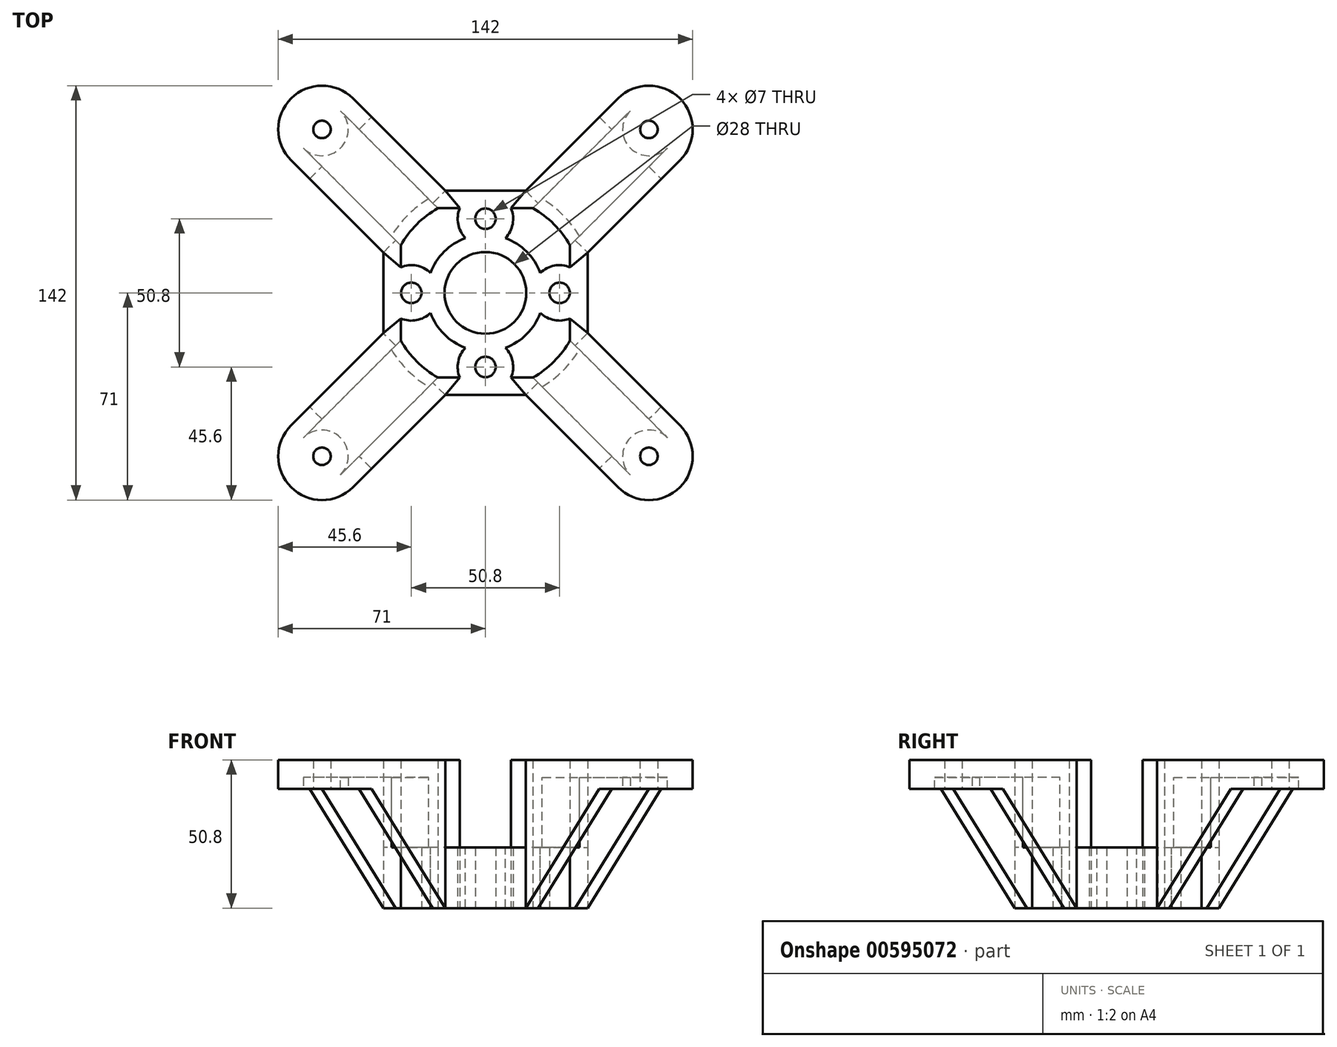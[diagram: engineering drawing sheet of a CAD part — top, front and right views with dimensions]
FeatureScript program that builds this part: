
annotation { "Feature Type Name" : "Feature", "Feature Type Description" : "" }
export const myFeature = defineFeature(function(context is Context, id is Id, definition is map)
    precondition{}
    {
        {
            var Q0;
            Q0=qCreatedBy(makeId("Top.planeOp"),FACE);
            var sketch = newSketch(context, id + "F0", { "sketchPlane" : qUnion([Q0])});
            skCircle(sketch, "E0", {"center": v(0, 0) * mm, "radius": 14 * mm});
            skCircle(sketch, "E1", {"center": v(0, 0) * mm, "radius": 25.4 * mm});
            skLineSegment(sketch, "E2", {"start": v(0, 0) * mm, "end": v(0, 25.4) * mm, "construction": true});
            skLineSegment(sketch, "E3", {"start": v(0, 0) * mm, "end": v(0, -25.4) * mm, "construction": true});
            skCircle(sketch, "E4", {"center": v(0, 25.4) * mm, "radius": 3.5 * mm});
            skLineSegment(sketch, "E5", {"start": v(0, 0) * mm, "end": v(25.4, 0) * mm, "construction": true});
            skCircle(sketch, "E6.MirrorC", {"center": v(0, -25.4) * mm, "radius": 3.5 * mm});
            skLineSegment(sketch, "E7.bottom", {"start": v(-35, 35) * mm, "end": v(35, 35) * mm});
            skLineSegment(sketch, "E7.top", {"start": v(-35, -35) * mm, "end": v(35, -35) * mm});
            skLineSegment(sketch, "E7.left", {"start": v(-35, 35) * mm, "end": v(-35, -35) * mm});
            skLineSegment(sketch, "E7.right", {"start": v(35, 35) * mm, "end": v(35, -35) * mm});
            skCircle(sketch, "E8", {"center": v(25.4, 0) * mm, "radius": 3.5 * mm});
            skCircle(sketch, "E9.MirrorC", {"center": v(-25.4, 0) * mm, "radius": 3.5 * mm});
            skLineSegment(sketch, "E10.bottom", {"start": v(-56, -56) * mm, "end": v(56, -56) * mm, "construction": true});
            skLineSegment(sketch, "E10.top", {"start": v(-56, 56) * mm, "end": v(56, 56) * mm, "construction": true});
            skLineSegment(sketch, "E10.left", {"start": v(-56, -56) * mm, "end": v(-56, 56) * mm, "construction": true});
            skLineSegment(sketch, "E10.right", {"start": v(56, -56) * mm, "end": v(56, 56) * mm, "construction": true});
            skLineSegment(sketch, "E11", {"start": v(0, 0) * mm, "end": v(-56, 56) * mm, "construction": true});
            skLineSegment(sketch, "E12.0", {"start": v(-13.79, 35) * mm, "end": v(-45.4, 66.6) * mm});
            skLineSegment(sketch, "E13.0", {"start": v(-35, 13.79) * mm, "end": v(-66.6, 45.4) * mm});
            skArc(sketch, "E14", {"start": v(-45.4, 66.6) * mm, "mid": v(-66.6, 66.6) * mm, "end": v(-66.6, 45.4) * mm});
            skCircle(sketch, "E15", {"center": v(-56, 56) * mm, "radius": 3 * mm});
            skLineSegment(sketch, "E16.MirrorCS", {"start": v(13.79, 35) * mm, "end": v(45.4, 66.6) * mm});
            skArc(sketch, "E17.MirrorCS", {"start": v(45.4, 66.6) * mm, "mid": v(66.6, 66.6) * mm, "end": v(66.6, 45.4) * mm});
            skLineSegment(sketch, "E18.MirrorCS", {"start": v(35, 13.79) * mm, "end": v(66.6, 45.4) * mm});
            skCircle(sketch, "E19.MirrorC", {"center": v(56, 56) * mm, "radius": 3 * mm});
            skLineSegment(sketch, "E20.MirrorCS", {"start": v(-13.79, -35) * mm, "end": v(-45.4, -66.6) * mm});
            skArc(sketch, "E21.MirrorCS", {"start": v(-45.4, -66.6) * mm, "mid": v(-66.6, -66.6) * mm, "end": v(-66.6, -45.4) * mm});
            skLineSegment(sketch, "E22.MirrorCS", {"start": v(-35, -13.79) * mm, "end": v(-66.6, -45.4) * mm});
            skCircle(sketch, "E23.MirrorC", {"center": v(-56, -56) * mm, "radius": 3 * mm});
            skCircle(sketch, "E24.MirrorC", {"center": v(56, -56) * mm, "radius": 3 * mm});
            skArc(sketch, "E25.MirrorCS", {"start": v(45.4, -66.6) * mm, "mid": v(66.6, -66.6) * mm, "end": v(66.6, -45.4) * mm});
            skLineSegment(sketch, "E26.MirrorCS", {"start": v(13.79, -35) * mm, "end": v(45.4, -66.6) * mm});
            skLineSegment(sketch, "E27.MirrorCS", {"start": v(35, -13.79) * mm, "end": v(66.6, -45.4) * mm});
            skSolve(sketch);
        }
        {
            var Q0;
            Q0=qSketchRegion(id+"F0",true);
            var Q1;
            Q1=makeQuery(id+"F0.imprint","IMPRINT",FACE,{"disambiguationData":[TD([[makeQuery(id+"F0.imprint","IMPRINT",EDGE,{"derivedFrom":sQuery(id+"F0.wireOp",EDGE,"E0")}),-1.0]])]});
            extrude(context, id + "F1", {"entities" : qUnion([Q0, Q1]), "depth" : 50.8 * mm});
        }
        {
            var Q0;
            Q0=makeQuery(id+"F1.opExtrude","CAP_FACE",FACE,{"disambiguationData":[OSD([sQuery(id+"F0.wireOp",EDGE,"E0"),sQuery(id+"F0.wireOp",EDGE,"E4"),sQuery(id+"F0.wireOp",EDGE,"E6.MirrorC"),sQuery(id+"F0.wireOp",EDGE,"E7.bottom"),sQuery(id+"F0.wireOp",EDGE,"E7.top"),sQuery(id+"F0.wireOp",EDGE,"E7.left"),sQuery(id+"F0.wireOp",EDGE,"E7.right"),sQuery(id+"F0.wireOp",EDGE,"E8"),sQuery(id+"F0.wireOp",EDGE,"E9.MirrorC"),sQuery(id+"F0.wireOp",EDGE,"E12.0"),sQuery(id+"F0.wireOp",EDGE,"E13.0"),sQuery(id+"F0.wireOp",EDGE,"E14"),sQuery(id+"F0.wireOp",EDGE,"E15"),sQuery(id+"F0.wireOp",EDGE,"E16.MirrorCS"),sQuery(id+"F0.wireOp",EDGE,"E17.MirrorCS"),sQuery(id+"F0.wireOp",EDGE,"E18.MirrorCS"),sQuery(id+"F0.wireOp",EDGE,"E19.MirrorC"),sQuery(id+"F0.wireOp",EDGE,"E20.MirrorCS"),sQuery(id+"F0.wireOp",EDGE,"E21.MirrorCS"),sQuery(id+"F0.wireOp",EDGE,"E22.MirrorCS"),sQuery(id+"F0.wireOp",EDGE,"E23.MirrorC"),sQuery(id+"F0.wireOp",EDGE,"E24.MirrorC"),sQuery(id+"F0.wireOp",EDGE,"E25.MirrorCS"),sQuery(id+"F0.wireOp",EDGE,"E26.MirrorCS"),sQuery(id+"F0.wireOp",EDGE,"E27.MirrorCS")])],"isStart":true});
            shell(context, id + "F2", {"entities" : qUnion([Q0]), "thickness" : 6 * mm});
        }
        {
            var Q0;
            Q0=makeQuery(id+"F1.opExtrude","SWEPT_FACE",FACE,{"disambiguationData":[OSD([sQuery(id+"F0.wireOp",EDGE,"E26.MirrorCS")])]});
            var sketch = newSketch(context, id + "F3", { "sketchPlane" : qUnion([Q0])});
            skLineSegment(sketch, "E28", {"start": v(94.2, 40.8) * mm, "end": v(94.2, 40.8) * mm});
            skLineSegment(sketch, "E29", {"start": v(94.2, 40.8) * mm, "end": v(34.5, 40.8) * mm});
            skLineSegment(sketch, "E30", {"start": v(34.5, 40.8) * mm, "end": v(34.5, 0) * mm});
            skPoint(sketch, "E31.0", {"position": v(94.2, 0) * mm});
            skPoint(sketch, "E32.0", {"position": v(94.2, 50.8) * mm});
            skLineSegment(sketch, "E33", {"start": v(34.5, 0) * mm, "end": v(94.2, 0) * mm});
            skPoint(sketch, "E34.0", {"position": v(70.2, 0) * mm});
            skLineSegment(sketch, "E35", {"start": v(70.2, 0) * mm, "end": v(70.2, 40.8) * mm});
            skLineSegment(sketch, "E36", {"start": v(70.2, 40.8) * mm, "end": v(34.5, 0) * mm});
            skLineSegment(sketch, "E37", {"start": v(94.2, 0) * mm, "end": v(94.2, 40.8) * mm});
            skSolve(sketch);
        }
        {
            var Q0;
            {var subQ0=sQuery(id+"F3.wireOp",EDGE,"E37");Q0=makeQuery(id+"F3.imprint","IMPRINT",FACE,{"disambiguationData":[TD([[makeQuery(id+"F3.imprint","IMPRINT",EDGE,{"derivedFrom":subQ0}),1.0]])]});}
            var Q1;
            {var subQ0=sQuery(id+"F3.wireOp",EDGE,"E35");Q1=makeQuery(id+"F3.imprint","IMPRINT",FACE,{"disambiguationData":[TD([[makeQuery(id+"F3.imprint","IMPRINT",EDGE,{"derivedFrom":subQ0}),-1.0]])]});}
            var Q2;
            {var subQ2=sQuery(id+"F3.wireOp",EDGE,"E35");Q2=makeQuery(id+"F3.imprint","IMPRINT",FACE,{"disambiguationData":[TD([[makeQuery(id+"F3.imprint","IMPRINT",EDGE,{"derivedFrom":subQ2}),1.0]])]});}
            extrude(context, id + "F4", {"entities" : qUnion([Q0, Q1, Q2]), "operationType" : NewBodyOperationType.REMOVE, "endBound" : BoundingType.THROUGH_ALL, "oppositeDirection" : true, "depth" : 25.4 * mm});
        }
        {
            var Q0;
            Q0=makeQuery(id+"F1.opExtrude","SWEPT_FACE",FACE,{"disambiguationData":[OSD([sQuery(id+"F0.wireOp",EDGE,"E18.MirrorCS")])]});
            var sketch = newSketch(context, id + "F5", { "sketchPlane" : qUnion([Q0])});
            skPoint(sketch, "E38.0", {"position": v(94.2, 0) * mm});
            skPoint(sketch, "E39.0", {"position": v(70.2, 0) * mm});
            skPoint(sketch, "E40.0", {"position": v(94.2, 50.8) * mm});
            skLineSegment(sketch, "E41", {"start": v(94.2, 0) * mm, "end": v(94.2, 40.8) * mm});
            skLineSegment(sketch, "E42", {"start": v(94.2, 0) * mm, "end": v(34.5, 0) * mm});
            skLineSegment(sketch, "E43", {"start": v(70.2, 0) * mm, "end": v(70.2, 40.8) * mm});
            skLineSegment(sketch, "E44", {"start": v(94.2, 40.8) * mm, "end": v(34.5, 40.8) * mm});
            skLineSegment(sketch, "E45", {"start": v(34.5, 40.8) * mm, "end": v(34.5, 0) * mm});
            skLineSegment(sketch, "E46", {"start": v(70.2, 40.8) * mm, "end": v(34.5, 0) * mm});
            skSolve(sketch);
        }
        {
            var Q0;
            {var subQ0=sQuery(id+"F5.wireOp",EDGE,"E41");Q0=makeQuery(id+"F5.imprint","IMPRINT",FACE,{"disambiguationData":[TD([[makeQuery(id+"F5.imprint","IMPRINT",EDGE,{"derivedFrom":subQ0}),1.0]])]});}
            var Q1;
            {var subQ3=sQuery(id+"F5.wireOp",EDGE,"E43");Q1=makeQuery(id+"F5.imprint","IMPRINT",FACE,{"disambiguationData":[TD([[makeQuery(id+"F5.imprint","IMPRINT",EDGE,{"derivedFrom":subQ3}),-1.0]])]});}
            var Q2;
            {var subQ2=sQuery(id+"F5.wireOp",EDGE,"E43");Q2=makeQuery(id+"F5.imprint","IMPRINT",FACE,{"disambiguationData":[TD([[makeQuery(id+"F5.imprint","IMPRINT",EDGE,{"derivedFrom":subQ2}),1.0]])]});}
            extrude(context, id + "F6", {"entities" : qUnion([Q0, Q1, Q2]), "operationType" : NewBodyOperationType.REMOVE, "endBound" : BoundingType.THROUGH_ALL, "oppositeDirection" : true, "depth" : 25.4 * mm});
        }
        {
            var Q0;
            Q0=makeQuery(id+"F1.opExtrude","SWEPT_FACE",FACE,{"disambiguationData":[OSD([sQuery(id+"F0.wireOp",EDGE,"E12.0")])]});
            var sketch = newSketch(context, id + "F7", { "sketchPlane" : qUnion([Q0])});
            skPoint(sketch, "E47.0", {"position": v(94.2, 0) * mm});
            skPoint(sketch, "E48.0", {"position": v(94.2, 50.8) * mm});
            skPoint(sketch, "E49.0", {"position": v(70.2, 0) * mm});
            skLineSegment(sketch, "E50", {"start": v(94.2, 0) * mm, "end": v(34.5, 0) * mm});
            skLineSegment(sketch, "E51", {"start": v(34.5, 0) * mm, "end": v(34.5, 40.8) * mm});
            skLineSegment(sketch, "E52", {"start": v(94.2, 0) * mm, "end": v(94.2, 40.8) * mm});
            skLineSegment(sketch, "E53", {"start": v(94.2, 40.8) * mm, "end": v(34.5, 40.8) * mm});
            skLineSegment(sketch, "E54", {"start": v(70.2, 0) * mm, "end": v(70.2, 40.8) * mm});
            skLineSegment(sketch, "E55", {"start": v(70.2, 40.8) * mm, "end": v(34.5, 0) * mm});
            skSolve(sketch);
        }
        {
            var Q0;
            {var subQ3=sQuery(id+"F7.wireOp",EDGE,"E52");Q0=makeQuery(id+"F7.imprint","IMPRINT",FACE,{"disambiguationData":[TD([[makeQuery(id+"F7.imprint","IMPRINT",EDGE,{"derivedFrom":subQ3}),1.0]])]});}
            var Q1;
            {var subQ3=sQuery(id+"F7.wireOp",EDGE,"E54");Q1=makeQuery(id+"F7.imprint","IMPRINT",FACE,{"disambiguationData":[TD([[makeQuery(id+"F7.imprint","IMPRINT",EDGE,{"derivedFrom":subQ3}),-1.0]])]});}
            var Q2;
            {var subQ2=sQuery(id+"F7.wireOp",EDGE,"E54");Q2=makeQuery(id+"F7.imprint","IMPRINT",FACE,{"disambiguationData":[TD([[makeQuery(id+"F7.imprint","IMPRINT",EDGE,{"derivedFrom":subQ2}),1.0]])]});}
            extrude(context, id + "F8", {"entities" : qUnion([Q0, Q1, Q2]), "operationType" : NewBodyOperationType.REMOVE, "endBound" : BoundingType.THROUGH_ALL, "oppositeDirection" : true, "depth" : 25.4 * mm});
        }
        {
            var Q0;
            Q0=makeQuery(id+"F1.opExtrude","SWEPT_FACE",FACE,{"disambiguationData":[OSD([sQuery(id+"F0.wireOp",EDGE,"E22.MirrorCS")])]});
            var sketch = newSketch(context, id + "F9", { "sketchPlane" : qUnion([Q0])});
            skPoint(sketch, "E56.0", {"position": v(94.2, 0) * mm});
            skPoint(sketch, "E56.1", {"position": v(70.2, 0) * mm});
            skPoint(sketch, "E56.2", {"position": v(94.2, 50.8) * mm});
            skLineSegment(sketch, "E57", {"start": v(94.2, 0) * mm, "end": v(34.5, 0) * mm});
            skLineSegment(sketch, "E58", {"start": v(34.5, 0) * mm, "end": v(34.5, 40.8) * mm});
            skLineSegment(sketch, "E59", {"start": v(94.2, 0) * mm, "end": v(94.2, 40.8) * mm});
            skLineSegment(sketch, "E60", {"start": v(94.2, 40.8) * mm, "end": v(34.5, 40.8) * mm});
            skLineSegment(sketch, "E61", {"start": v(70.2, 0) * mm, "end": v(70.2, 40.8) * mm});
            skLineSegment(sketch, "E62", {"start": v(70.2, 40.8) * mm, "end": v(34.5, 0) * mm});
            skSolve(sketch);
        }
        {
            var Q0;
            {var subQ2=sQuery(id+"F9.wireOp",EDGE,"E61");Q0=makeQuery(id+"F9.imprint","IMPRINT",FACE,{"disambiguationData":[TD([[makeQuery(id+"F9.imprint","IMPRINT",EDGE,{"derivedFrom":subQ2}),1.0]])]});}
            var Q1;
            {var subQ3=sQuery(id+"F9.wireOp",EDGE,"E61");Q1=makeQuery(id+"F9.imprint","IMPRINT",FACE,{"disambiguationData":[TD([[makeQuery(id+"F9.imprint","IMPRINT",EDGE,{"derivedFrom":subQ3}),-1.0]])]});}
            var Q2;
            {var subQ3=sQuery(id+"F9.wireOp",EDGE,"E59");Q2=makeQuery(id+"F9.imprint","IMPRINT",FACE,{"disambiguationData":[TD([[makeQuery(id+"F9.imprint","IMPRINT",EDGE,{"derivedFrom":subQ3}),1.0]])]});}
            extrude(context, id + "F10", {"entities" : qUnion([Q0, Q1, Q2]), "operationType" : NewBodyOperationType.REMOVE, "endBound" : BoundingType.THROUGH_ALL, "oppositeDirection" : true, "depth" : 25.4 * mm});
        }
        {
            var Q0;
            Q0=makeQuery(id+"F1.opExtrude","CAP_FACE",FACE,{"disambiguationData":[OSD([sQuery(id+"F0.wireOp",EDGE,"E0"),sQuery(id+"F0.wireOp",EDGE,"E4"),sQuery(id+"F0.wireOp",EDGE,"E6.MirrorC"),sQuery(id+"F0.wireOp",EDGE,"E7.bottom"),sQuery(id+"F0.wireOp",EDGE,"E7.top"),sQuery(id+"F0.wireOp",EDGE,"E7.left"),sQuery(id+"F0.wireOp",EDGE,"E7.right"),sQuery(id+"F0.wireOp",EDGE,"E8"),sQuery(id+"F0.wireOp",EDGE,"E9.MirrorC"),sQuery(id+"F0.wireOp",EDGE,"E12.0"),sQuery(id+"F0.wireOp",EDGE,"E13.0"),sQuery(id+"F0.wireOp",EDGE,"E14"),sQuery(id+"F0.wireOp",EDGE,"E15"),sQuery(id+"F0.wireOp",EDGE,"E16.MirrorCS"),sQuery(id+"F0.wireOp",EDGE,"E17.MirrorCS"),sQuery(id+"F0.wireOp",EDGE,"E18.MirrorCS"),sQuery(id+"F0.wireOp",EDGE,"E19.MirrorC"),sQuery(id+"F0.wireOp",EDGE,"E20.MirrorCS"),sQuery(id+"F0.wireOp",EDGE,"E21.MirrorCS"),sQuery(id+"F0.wireOp",EDGE,"E22.MirrorCS"),sQuery(id+"F0.wireOp",EDGE,"E23.MirrorC"),sQuery(id+"F0.wireOp",EDGE,"E24.MirrorC"),sQuery(id+"F0.wireOp",EDGE,"E25.MirrorCS"),sQuery(id+"F0.wireOp",EDGE,"E26.MirrorCS"),sQuery(id+"F0.wireOp",EDGE,"E27.MirrorCS")])],"isStart":false});
            var sketch = newSketch(context, id + "F11", { "sketchPlane" : qUnion([Q0])});
            skLineSegment(sketch, "E63.bottom", {"start": v(35, 35) * mm, "end": v(-35, 35) * mm});
            skLineSegment(sketch, "E63.top", {"start": v(35, -35) * mm, "end": v(-35, -35) * mm});
            skLineSegment(sketch, "E63.left", {"start": v(35, 35) * mm, "end": v(35, -35) * mm});
            skLineSegment(sketch, "E63.right", {"start": v(-35, 35) * mm, "end": v(-35, -35) * mm});
            skPoint(sketch, "E63.middle", {"position": v(0, 0) * mm});
            skPoint(sketch, "E64.0", {"position": v(-13.79, 35) * mm});
            skPoint(sketch, "E65.0", {"position": v(13.79, 35) * mm});
            skPoint(sketch, "E66.0", {"position": v(35, 13.79) * mm});
            skPoint(sketch, "E67.0", {"position": v(35, -13.79) * mm});
            skPoint(sketch, "E68.0", {"position": v(-35, 13.79) * mm});
            skPoint(sketch, "E69.0", {"position": v(-35, -13.79) * mm});
            skPoint(sketch, "E70.0", {"position": v(-13.79, -35) * mm});
            skPoint(sketch, "E71.0", {"position": v(13.79, -35) * mm});
            skCircle(sketch, "E72", {"center": v(0, 0) * mm, "radius": 37.62 * mm});
            skSolve(sketch);
        }
        {
            var Q0;
            Q0=makeQuery(id+"F11.imprint","IMPRINT",FACE,{"disambiguationData":[TD([[makeQuery(id+"F11.imprint","IMPRINT",EDGE,{"derivedFrom":makeQuery(id+"F1.opExtrude","CAP_EDGE",EDGE,{"disambiguationData":[OSD([sQuery(id+"F0.wireOp",EDGE,"E0")])],"isStart":false})}),-1.0]])]});
            extrude(context, id + "F12", {"entities" : qUnion([Q0]), "operationType" : NewBodyOperationType.REMOVE, "oppositeDirection" : true, "depth" : 30 * mm});
        }
        {
            var Q0;
            Q0=makeQuery(id+"F12.boolean.opBoolean","COPY",FACE,{"derivedFrom":makeQuery(id+"F12.opExtrude","CAP_FACE",FACE,{"disambiguationData":[OSD([sQuery(id+"F0.wireOp",EDGE,"E0"),sQuery(id+"F0.wireOp",EDGE,"E4"),sQuery(id+"F0.wireOp",EDGE,"E6.MirrorC"),sQuery(id+"F0.wireOp",EDGE,"E8"),sQuery(id+"F0.wireOp",EDGE,"E9.MirrorC"),sQuery(id+"F11.wireOp",EDGE,"E63.bottom"),sQuery(id+"F11.wireOp",EDGE,"E63.top"),sQuery(id+"F11.wireOp",EDGE,"E63.left"),sQuery(id+"F11.wireOp",EDGE,"E63.right"),sQuery(id+"F11.wireOp",EDGE,"E72")])],"isStart":false})});
            var sketch = newSketch(context, id + "F13", { "sketchPlane" : qUnion([Q0])});
            skCircle(sketch, "E73", {"center": v(0, 0) * mm, "radius": 37.62 * mm});
            skCircle(sketch, "E74", {"center": v(0, 0) * mm, "radius": 33.25 * mm});
            skLineSegment(sketch, "E75", {"start": v(-13.79, 35) * mm, "end": v(-8.8, 29) * mm});
            skLineSegment(sketch, "E76", {"start": v(8.8, 29) * mm, "end": v(13.79, 35) * mm});
            skLineSegment(sketch, "E77", {"start": v(-29, 8.8) * mm, "end": v(-35, 13.79) * mm});
            skLineSegment(sketch, "E78", {"start": v(29, 8.8) * mm, "end": v(35, 13.79) * mm});
            skLineSegment(sketch, "E79", {"start": v(29, -8.8) * mm, "end": v(35, -13.79) * mm});
            skLineSegment(sketch, "E80", {"start": v(8.8, -29) * mm, "end": v(13.79, -35) * mm});
            skLineSegment(sketch, "E81", {"start": v(-8.8, -29) * mm, "end": v(-13.79, -35) * mm});
            skLineSegment(sketch, "E82", {"start": v(-29, -8.8) * mm, "end": v(-35, -13.79) * mm});
            skSolve(sketch);
        }
        {
            var Q0;
            {var subQ1=makeQuery(id+"F12.opExtrude","CAP_FACE",FACE,{"disambiguationData":[OSD([sQuery(id+"F0.wireOp",EDGE,"E0"),sQuery(id+"F0.wireOp",EDGE,"E4"),sQuery(id+"F0.wireOp",EDGE,"E6.MirrorC"),sQuery(id+"F0.wireOp",EDGE,"E8"),sQuery(id+"F0.wireOp",EDGE,"E9.MirrorC"),sQuery(id+"F11.wireOp",EDGE,"E63.bottom"),sQuery(id+"F11.wireOp",EDGE,"E63.top"),sQuery(id+"F11.wireOp",EDGE,"E63.left"),sQuery(id+"F11.wireOp",EDGE,"E63.right"),sQuery(id+"F11.wireOp",EDGE,"E72")])],"isStart":false});var subQ2=makeQuery(id+"F12.boolean.opBoolean","INTERSECT",EDGE,{"derivedFrom":[makeQuery(id+"F2.opShell","OFFSET_FACE",FACE,{"disambiguationData":[OSD([sQuery(id+"F0.wireOp",EDGE,"E26.MirrorCS")])]}),subQ1]});Q0=makeQuery(id+"F13.imprint","IMPRINT",FACE,{"disambiguationData":[TD([[makeQuery(id+"F13.imprint","IMPRINT",EDGE,{"derivedFrom":subQ2}),1.0]])]});}
            var Q1;
            {var subQ0=sQuery(id+"F13.wireOp",EDGE,"E80");var subQ6=sQuery(id+"F13.wireOp",EDGE,"E74");var subQ7=makeQuery(id+"F13.imprint","INTERSECT",VERTEX,{"derivedFrom":[subQ6,subQ0]});Q1=makeQuery(id+"F13.imprint","IMPRINT",FACE,{"disambiguationData":[TD([[makeQuery(id+"F13.imprint","IMPRINT",EDGE,{"disambiguationData":[TD([[subQ7,-1.0]])],"derivedFrom":subQ0}),1.0]])]});}
            var Q2;
            {var subQ0=sQuery(id+"F13.wireOp",EDGE,"E79");var subQ6=sQuery(id+"F13.wireOp",EDGE,"E74");var subQ7=makeQuery(id+"F13.imprint","INTERSECT",VERTEX,{"derivedFrom":[subQ6,subQ0]});Q2=makeQuery(id+"F13.imprint","IMPRINT",FACE,{"disambiguationData":[TD([[makeQuery(id+"F13.imprint","IMPRINT",EDGE,{"disambiguationData":[TD([[subQ7,-1.0]])],"derivedFrom":subQ0}),-1.0]])]});}
            var Q3;
            {var subQ0=sQuery(id+"F13.wireOp",EDGE,"E81");var subQ6=sQuery(id+"F13.wireOp",EDGE,"E74");var subQ7=makeQuery(id+"F13.imprint","INTERSECT",VERTEX,{"derivedFrom":[subQ6,subQ0]});Q3=makeQuery(id+"F13.imprint","IMPRINT",FACE,{"disambiguationData":[TD([[makeQuery(id+"F13.imprint","IMPRINT",EDGE,{"disambiguationData":[TD([[subQ7,-1.0]])],"derivedFrom":subQ0}),-1.0]])]});}
            var Q4;
            {var subQ1=makeQuery(id+"F12.opExtrude","CAP_FACE",FACE,{"disambiguationData":[OSD([sQuery(id+"F0.wireOp",EDGE,"E0"),sQuery(id+"F0.wireOp",EDGE,"E4"),sQuery(id+"F0.wireOp",EDGE,"E6.MirrorC"),sQuery(id+"F0.wireOp",EDGE,"E8"),sQuery(id+"F0.wireOp",EDGE,"E9.MirrorC"),sQuery(id+"F11.wireOp",EDGE,"E63.bottom"),sQuery(id+"F11.wireOp",EDGE,"E63.top"),sQuery(id+"F11.wireOp",EDGE,"E63.left"),sQuery(id+"F11.wireOp",EDGE,"E63.right"),sQuery(id+"F11.wireOp",EDGE,"E72")])],"isStart":false});var subQ2=makeQuery(id+"F12.boolean.opBoolean","INTERSECT",EDGE,{"derivedFrom":[makeQuery(id+"F2.opShell","OFFSET_FACE",FACE,{"disambiguationData":[OSD([sQuery(id+"F0.wireOp",EDGE,"E20.MirrorCS")])]}),subQ1]});Q4=makeQuery(id+"F13.imprint","IMPRINT",FACE,{"disambiguationData":[TD([[makeQuery(id+"F13.imprint","IMPRINT",EDGE,{"derivedFrom":subQ2}),-1.0]])]});}
            var Q5;
            {var subQ0=sQuery(id+"F13.wireOp",EDGE,"E82");var subQ6=sQuery(id+"F13.wireOp",EDGE,"E74");var subQ7=makeQuery(id+"F13.imprint","INTERSECT",VERTEX,{"derivedFrom":[subQ6,subQ0]});Q5=makeQuery(id+"F13.imprint","IMPRINT",FACE,{"disambiguationData":[TD([[makeQuery(id+"F13.imprint","IMPRINT",EDGE,{"disambiguationData":[TD([[subQ7,-1.0]])],"derivedFrom":subQ0}),1.0]])]});}
            var Q6;
            {var subQ1=sQuery(id+"F0.wireOp",EDGE,"E8");var subQ2=makeQuery(id+"F12.opExtrude","CAP_FACE",FACE,{"disambiguationData":[OSD([sQuery(id+"F0.wireOp",EDGE,"E0"),sQuery(id+"F0.wireOp",EDGE,"E4"),sQuery(id+"F0.wireOp",EDGE,"E6.MirrorC"),subQ1,sQuery(id+"F0.wireOp",EDGE,"E9.MirrorC"),sQuery(id+"F11.wireOp",EDGE,"E63.bottom"),sQuery(id+"F11.wireOp",EDGE,"E63.top"),sQuery(id+"F11.wireOp",EDGE,"E63.left"),sQuery(id+"F11.wireOp",EDGE,"E63.right"),sQuery(id+"F11.wireOp",EDGE,"E72")])],"isStart":false});var subQ3=makeQuery(id+"F12.boolean.opBoolean","INTERSECT",EDGE,{"derivedFrom":[makeQuery(id+"F2.opShell","OFFSET_FACE",FACE,{"disambiguationData":[OSD([sQuery(id+"F0.wireOp",EDGE,"E7.right")]),OD(1.0)]}),subQ2]});Q6=makeQuery(id+"F13.imprint","IMPRINT",FACE,{"disambiguationData":[TD([[makeQuery(id+"F13.imprint","IMPRINT",EDGE,{"derivedFrom":subQ3}),1.0]])]});}
            var Q7;
            {var subQ1=sQuery(id+"F0.wireOp",EDGE,"E6.MirrorC");var subQ2=makeQuery(id+"F12.opExtrude","CAP_FACE",FACE,{"disambiguationData":[OSD([sQuery(id+"F0.wireOp",EDGE,"E0"),sQuery(id+"F0.wireOp",EDGE,"E4"),subQ1,sQuery(id+"F0.wireOp",EDGE,"E8"),sQuery(id+"F0.wireOp",EDGE,"E9.MirrorC"),sQuery(id+"F11.wireOp",EDGE,"E63.bottom"),sQuery(id+"F11.wireOp",EDGE,"E63.top"),sQuery(id+"F11.wireOp",EDGE,"E63.left"),sQuery(id+"F11.wireOp",EDGE,"E63.right"),sQuery(id+"F11.wireOp",EDGE,"E72")])],"isStart":false});var subQ3=makeQuery(id+"F12.boolean.opBoolean","INTERSECT",EDGE,{"derivedFrom":[makeQuery(id+"F2.opShell","OFFSET_FACE",FACE,{"disambiguationData":[OSD([sQuery(id+"F0.wireOp",EDGE,"E7.top")]),OD(1.0)]}),subQ2]});Q7=makeQuery(id+"F13.imprint","IMPRINT",FACE,{"disambiguationData":[TD([[makeQuery(id+"F13.imprint","IMPRINT",EDGE,{"derivedFrom":subQ3}),-1.0]])]});}
            var Q8;
            {var subQ1=sQuery(id+"F0.wireOp",EDGE,"E6.MirrorC");var subQ2=makeQuery(id+"F12.opExtrude","CAP_FACE",FACE,{"disambiguationData":[OSD([sQuery(id+"F0.wireOp",EDGE,"E0"),sQuery(id+"F0.wireOp",EDGE,"E4"),subQ1,sQuery(id+"F0.wireOp",EDGE,"E8"),sQuery(id+"F0.wireOp",EDGE,"E9.MirrorC"),sQuery(id+"F11.wireOp",EDGE,"E63.bottom"),sQuery(id+"F11.wireOp",EDGE,"E63.top"),sQuery(id+"F11.wireOp",EDGE,"E63.left"),sQuery(id+"F11.wireOp",EDGE,"E63.right"),sQuery(id+"F11.wireOp",EDGE,"E72")])],"isStart":false});var subQ3=makeQuery(id+"F12.boolean.opBoolean","INTERSECT",EDGE,{"derivedFrom":[makeQuery(id+"F2.opShell","OFFSET_FACE",FACE,{"disambiguationData":[OSD([sQuery(id+"F0.wireOp",EDGE,"E7.top")]),OD(0.0)]}),subQ2]});Q8=makeQuery(id+"F13.imprint","IMPRINT",FACE,{"disambiguationData":[TD([[makeQuery(id+"F13.imprint","IMPRINT",EDGE,{"derivedFrom":subQ3}),-1.0]])]});}
            var Q9;
            {var subQ1=sQuery(id+"F0.wireOp",EDGE,"E9.MirrorC");var subQ2=makeQuery(id+"F12.opExtrude","CAP_FACE",FACE,{"disambiguationData":[OSD([sQuery(id+"F0.wireOp",EDGE,"E0"),sQuery(id+"F0.wireOp",EDGE,"E4"),sQuery(id+"F0.wireOp",EDGE,"E6.MirrorC"),sQuery(id+"F0.wireOp",EDGE,"E8"),subQ1,sQuery(id+"F11.wireOp",EDGE,"E63.bottom"),sQuery(id+"F11.wireOp",EDGE,"E63.top"),sQuery(id+"F11.wireOp",EDGE,"E63.left"),sQuery(id+"F11.wireOp",EDGE,"E63.right"),sQuery(id+"F11.wireOp",EDGE,"E72")])],"isStart":false});var subQ3=makeQuery(id+"F12.boolean.opBoolean","INTERSECT",EDGE,{"derivedFrom":[makeQuery(id+"F2.opShell","OFFSET_FACE",FACE,{"disambiguationData":[OSD([sQuery(id+"F0.wireOp",EDGE,"E7.left")]),OD(1.0)]}),subQ2]});Q9=makeQuery(id+"F13.imprint","IMPRINT",FACE,{"disambiguationData":[TD([[makeQuery(id+"F13.imprint","IMPRINT",EDGE,{"derivedFrom":subQ3}),-1.0]])]});}
            var Q10;
            {var subQ1=sQuery(id+"F0.wireOp",EDGE,"E9.MirrorC");var subQ2=makeQuery(id+"F12.opExtrude","CAP_FACE",FACE,{"disambiguationData":[OSD([sQuery(id+"F0.wireOp",EDGE,"E0"),sQuery(id+"F0.wireOp",EDGE,"E4"),sQuery(id+"F0.wireOp",EDGE,"E6.MirrorC"),sQuery(id+"F0.wireOp",EDGE,"E8"),subQ1,sQuery(id+"F11.wireOp",EDGE,"E63.bottom"),sQuery(id+"F11.wireOp",EDGE,"E63.top"),sQuery(id+"F11.wireOp",EDGE,"E63.left"),sQuery(id+"F11.wireOp",EDGE,"E63.right"),sQuery(id+"F11.wireOp",EDGE,"E72")])],"isStart":false});var subQ3=makeQuery(id+"F12.boolean.opBoolean","INTERSECT",EDGE,{"derivedFrom":[makeQuery(id+"F2.opShell","OFFSET_FACE",FACE,{"disambiguationData":[OSD([sQuery(id+"F0.wireOp",EDGE,"E7.left")]),OD(0.0)]}),subQ2]});Q10=makeQuery(id+"F13.imprint","IMPRINT",FACE,{"disambiguationData":[TD([[makeQuery(id+"F13.imprint","IMPRINT",EDGE,{"derivedFrom":subQ3}),-1.0]])]});}
            var Q11;
            {var subQ0=sQuery(id+"F13.wireOp",EDGE,"E77");var subQ6=sQuery(id+"F13.wireOp",EDGE,"E74");var subQ7=makeQuery(id+"F13.imprint","INTERSECT",VERTEX,{"derivedFrom":[subQ6,subQ0]});Q11=makeQuery(id+"F13.imprint","IMPRINT",FACE,{"disambiguationData":[TD([[makeQuery(id+"F13.imprint","IMPRINT",EDGE,{"disambiguationData":[TD([[subQ7,-1.0]])],"derivedFrom":subQ0}),-1.0]])]});}
            var Q12;
            {var subQ1=makeQuery(id+"F12.opExtrude","CAP_FACE",FACE,{"disambiguationData":[OSD([sQuery(id+"F0.wireOp",EDGE,"E0"),sQuery(id+"F0.wireOp",EDGE,"E4"),sQuery(id+"F0.wireOp",EDGE,"E6.MirrorC"),sQuery(id+"F0.wireOp",EDGE,"E8"),sQuery(id+"F0.wireOp",EDGE,"E9.MirrorC"),sQuery(id+"F11.wireOp",EDGE,"E63.bottom"),sQuery(id+"F11.wireOp",EDGE,"E63.top"),sQuery(id+"F11.wireOp",EDGE,"E63.left"),sQuery(id+"F11.wireOp",EDGE,"E63.right"),sQuery(id+"F11.wireOp",EDGE,"E72")])],"isStart":false});var subQ2=makeQuery(id+"F12.boolean.opBoolean","INTERSECT",EDGE,{"derivedFrom":[makeQuery(id+"F2.opShell","OFFSET_FACE",FACE,{"disambiguationData":[OSD([sQuery(id+"F0.wireOp",EDGE,"E12.0")])]}),subQ1]});Q12=makeQuery(id+"F13.imprint","IMPRINT",FACE,{"disambiguationData":[TD([[makeQuery(id+"F13.imprint","IMPRINT",EDGE,{"derivedFrom":subQ2}),1.0]])]});}
            var Q13;
            {var subQ0=sQuery(id+"F13.wireOp",EDGE,"E75");var subQ6=sQuery(id+"F13.wireOp",EDGE,"E74");var subQ7=makeQuery(id+"F13.imprint","INTERSECT",VERTEX,{"derivedFrom":[subQ6,subQ0]});Q13=makeQuery(id+"F13.imprint","IMPRINT",FACE,{"disambiguationData":[TD([[makeQuery(id+"F13.imprint","IMPRINT",EDGE,{"disambiguationData":[TD([[subQ7,1.0]])],"derivedFrom":subQ0}),-1.0]])]});}
            var Q14;
            {var subQ1=sQuery(id+"F0.wireOp",EDGE,"E4");var subQ2=makeQuery(id+"F12.opExtrude","CAP_FACE",FACE,{"disambiguationData":[OSD([sQuery(id+"F0.wireOp",EDGE,"E0"),subQ1,sQuery(id+"F0.wireOp",EDGE,"E6.MirrorC"),sQuery(id+"F0.wireOp",EDGE,"E8"),sQuery(id+"F0.wireOp",EDGE,"E9.MirrorC"),sQuery(id+"F11.wireOp",EDGE,"E63.bottom"),sQuery(id+"F11.wireOp",EDGE,"E63.top"),sQuery(id+"F11.wireOp",EDGE,"E63.left"),sQuery(id+"F11.wireOp",EDGE,"E63.right"),sQuery(id+"F11.wireOp",EDGE,"E72")])],"isStart":false});var subQ3=makeQuery(id+"F12.boolean.opBoolean","INTERSECT",EDGE,{"derivedFrom":[makeQuery(id+"F2.opShell","OFFSET_FACE",FACE,{"disambiguationData":[OSD([sQuery(id+"F0.wireOp",EDGE,"E7.bottom")]),OD(0.0)]}),subQ2]});Q14=makeQuery(id+"F13.imprint","IMPRINT",FACE,{"disambiguationData":[TD([[makeQuery(id+"F13.imprint","IMPRINT",EDGE,{"derivedFrom":subQ3}),1.0]])]});}
            var Q15;
            {var subQ1=sQuery(id+"F0.wireOp",EDGE,"E4");var subQ2=makeQuery(id+"F12.opExtrude","CAP_FACE",FACE,{"disambiguationData":[OSD([sQuery(id+"F0.wireOp",EDGE,"E0"),subQ1,sQuery(id+"F0.wireOp",EDGE,"E6.MirrorC"),sQuery(id+"F0.wireOp",EDGE,"E8"),sQuery(id+"F0.wireOp",EDGE,"E9.MirrorC"),sQuery(id+"F11.wireOp",EDGE,"E63.bottom"),sQuery(id+"F11.wireOp",EDGE,"E63.top"),sQuery(id+"F11.wireOp",EDGE,"E63.left"),sQuery(id+"F11.wireOp",EDGE,"E63.right"),sQuery(id+"F11.wireOp",EDGE,"E72")])],"isStart":false});var subQ3=makeQuery(id+"F12.boolean.opBoolean","INTERSECT",EDGE,{"derivedFrom":[makeQuery(id+"F2.opShell","OFFSET_FACE",FACE,{"disambiguationData":[OSD([sQuery(id+"F0.wireOp",EDGE,"E7.bottom")]),OD(1.0)]}),subQ2]});Q15=makeQuery(id+"F13.imprint","IMPRINT",FACE,{"disambiguationData":[TD([[makeQuery(id+"F13.imprint","IMPRINT",EDGE,{"derivedFrom":subQ3}),1.0]])]});}
            var Q16;
            {var subQ0=sQuery(id+"F13.wireOp",EDGE,"E76");var subQ6=sQuery(id+"F13.wireOp",EDGE,"E74");var subQ7=makeQuery(id+"F13.imprint","INTERSECT",VERTEX,{"derivedFrom":[subQ6,subQ0]});Q16=makeQuery(id+"F13.imprint","IMPRINT",FACE,{"disambiguationData":[TD([[makeQuery(id+"F13.imprint","IMPRINT",EDGE,{"disambiguationData":[TD([[subQ7,-1.0]])],"derivedFrom":subQ0}),-1.0]])]});}
            var Q17;
            {var subQ1=makeQuery(id+"F12.opExtrude","CAP_FACE",FACE,{"disambiguationData":[OSD([sQuery(id+"F0.wireOp",EDGE,"E0"),sQuery(id+"F0.wireOp",EDGE,"E4"),sQuery(id+"F0.wireOp",EDGE,"E6.MirrorC"),sQuery(id+"F0.wireOp",EDGE,"E8"),sQuery(id+"F0.wireOp",EDGE,"E9.MirrorC"),sQuery(id+"F11.wireOp",EDGE,"E63.bottom"),sQuery(id+"F11.wireOp",EDGE,"E63.top"),sQuery(id+"F11.wireOp",EDGE,"E63.left"),sQuery(id+"F11.wireOp",EDGE,"E63.right"),sQuery(id+"F11.wireOp",EDGE,"E72")])],"isStart":false});var subQ2=makeQuery(id+"F12.boolean.opBoolean","INTERSECT",EDGE,{"derivedFrom":[makeQuery(id+"F2.opShell","OFFSET_FACE",FACE,{"disambiguationData":[OSD([sQuery(id+"F0.wireOp",EDGE,"E16.MirrorCS")])]}),subQ1]});Q17=makeQuery(id+"F13.imprint","IMPRINT",FACE,{"disambiguationData":[TD([[makeQuery(id+"F13.imprint","IMPRINT",EDGE,{"derivedFrom":subQ2}),-1.0]])]});}
            var Q18;
            {var subQ0=sQuery(id+"F13.wireOp",EDGE,"E78");var subQ6=sQuery(id+"F13.wireOp",EDGE,"E74");var subQ7=makeQuery(id+"F13.imprint","INTERSECT",VERTEX,{"derivedFrom":[subQ6,subQ0]});Q18=makeQuery(id+"F13.imprint","IMPRINT",FACE,{"disambiguationData":[TD([[makeQuery(id+"F13.imprint","IMPRINT",EDGE,{"disambiguationData":[TD([[subQ7,-1.0]])],"derivedFrom":subQ0}),1.0]])]});}
            var Q19;
            {var subQ1=sQuery(id+"F0.wireOp",EDGE,"E8");var subQ2=makeQuery(id+"F12.opExtrude","CAP_FACE",FACE,{"disambiguationData":[OSD([sQuery(id+"F0.wireOp",EDGE,"E0"),sQuery(id+"F0.wireOp",EDGE,"E4"),sQuery(id+"F0.wireOp",EDGE,"E6.MirrorC"),subQ1,sQuery(id+"F0.wireOp",EDGE,"E9.MirrorC"),sQuery(id+"F11.wireOp",EDGE,"E63.bottom"),sQuery(id+"F11.wireOp",EDGE,"E63.top"),sQuery(id+"F11.wireOp",EDGE,"E63.left"),sQuery(id+"F11.wireOp",EDGE,"E63.right"),sQuery(id+"F11.wireOp",EDGE,"E72")])],"isStart":false});var subQ3=makeQuery(id+"F12.boolean.opBoolean","INTERSECT",EDGE,{"derivedFrom":[makeQuery(id+"F2.opShell","OFFSET_FACE",FACE,{"disambiguationData":[OSD([sQuery(id+"F0.wireOp",EDGE,"E7.right")]),OD(0.0)]}),subQ2]});Q19=makeQuery(id+"F13.imprint","IMPRINT",FACE,{"disambiguationData":[TD([[makeQuery(id+"F13.imprint","IMPRINT",EDGE,{"derivedFrom":subQ3}),1.0]])]});}
            extrude(context, id + "F14", {"entities" : qUnion([Q0, Q1, Q2, Q3, Q4, Q5, Q6, Q7, Q8, Q9, Q10, Q11, Q12, Q13, Q14, Q15, Q16, Q17, Q18, Q19]), "operationType" : NewBodyOperationType.ADD, "depth" : 30 * mm});
        }
    });
